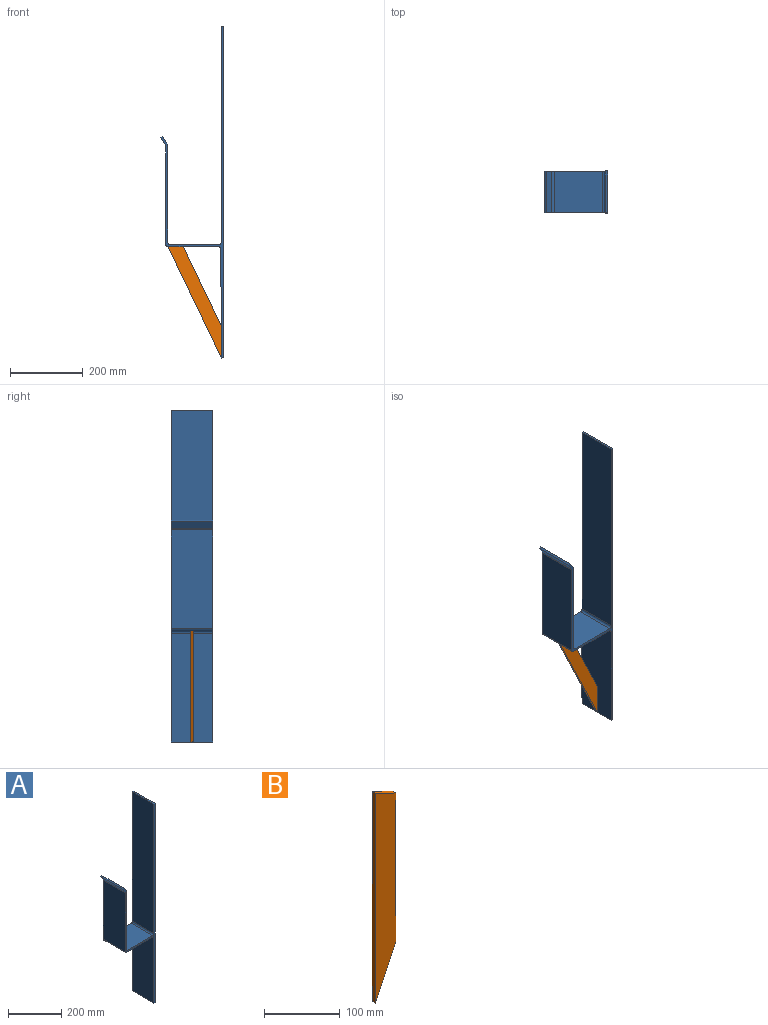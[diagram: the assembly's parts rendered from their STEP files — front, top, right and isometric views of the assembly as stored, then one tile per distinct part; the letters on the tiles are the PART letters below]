
ASSEMBLY  parts=2 mates=1
PART A: 20 faces, bbox 173.9x114.3x914.4 mm
  f0: plane 300.16x114.3mm, normal (-1,0,0), area 34308.5mm2, adj f1,f17,f18,f19
  f1: plane 114.3x6.35mm, normal (0,0,-1), area 725.8mm2, adj f0,f2,f18,f19
  f2: plane 914.4x114.3mm, normal (1,0,0), area 104515.9mm2, adj f1,f3,f18,f19
  f3: plane 114.3x6.35mm, normal (0,0,1), area 725.8mm2, adj f2,f4,f18,f19
  f4: plane 595.21x114.3mm, normal (-1,0,0), area 68032.9mm2, adj f3,f5,f18,f19
  f5: cylinder r=6.35mm len=114.3mm, axis (0,1,0), area 1140.1mm2, adj f4,f6,f18,f19
  f6: plane 134.47x114.3mm, normal (0,0,1), area 15369.3mm2, adj f5,f7,f18,f19
  f7: cylinder r=6.35mm len=114.3mm, axis (0,1,0), area 1140.1mm2, adj f6,f8,f18,f19
  f8: plane 266.7x114.3mm, normal (1,0,0), area 30483.8mm2, adj f7,f9,f18,f19
  f9: cylinder r=6.35mm len=114.3mm, axis (0,1,0), area 423.9mm2, adj f8,f10,f18,f19
  f10: plane 114.3x21.19mm, normal (0.83,0,0.55), area 2903.2mm2, adj f9,f11,f18,f19
  f11: plane 114.3x5.3mm, normal (-0.55,0,0.83), area 725.8mm2, adj f10,f12,f18,f19
  f12: plane 114.3x19.6mm, normal (-0.83,0,-0.55), area 2685.1mm2, adj f11,f13,f18,f19
  f13: cylinder r=6.35mm len=114.3mm, axis (0,1,0), area 423.9mm2, adj f12,f14,f18,f19
  f14: plane 271.14x114.3mm, normal (-1,0,0), area 30991.4mm2, adj f13,f15,f18,f19
  f15: cylinder r=6.35mm len=114.3mm, axis (0,1,0), area 1140.1mm2, adj f14,f16,f18,f19
  f16: plane 139.72x114.3mm, normal (0,0,-1), area 15970.3mm2, adj f15,f17,f18,f19
  f17: cylinder r=6.35mm len=114.3mm, axis (0,1,0), area 1137.5mm2, adj f0,f16,f18,f19
  f18: plane 914.4x173.87mm, normal (0,-1,0), area 8876.6mm2, adj f0,f1,f2,f3,f4,f5,f6,f7
  f19: plane 914.4x173.87mm, normal (0,1,0), area 8876.6mm2, adj f0,f1,f2,f3,f4,f5,f6,f7
PART B: 6 faces, bbox 38.1x6.4x340 mm
  f0: plane 38.1x18.29mm, normal (0.43,0,0.9), area 268.4mm2, adj f1,f3,f4,f5
  f1: plane 339.98x6.35mm, normal (-1,0,0), area 2158.9mm2, adj f0,f2,f4,f5
  f2: plane 80.09x38.1mm, normal (0.9,0,-0.43), area 563.2mm2, adj f1,f3,f4,f5
  f3: plane 241.59x6.35mm, normal (1,0,0), area 1534.1mm2, adj f0,f2,f4,f5
  f4: plane 339.98x38.1mm, normal (0,-1,0), area 11078.9mm2, adj f0,f1,f2,f3
  f5: plane 339.98x38.1mm, normal (0,1,0), area 11078.9mm2, adj f0,f1,f2,f3
PLACE A t=(-327.96,120.32,-3.13)mm
PLACE B rot(axis=(0,-1,0),25.6deg) t=(-390.73,66.34,158.36)mm
MATE fastened B.f0 <-> A.f16  axis (0,0,1) through (-481.48,63.17,303.35)mm
